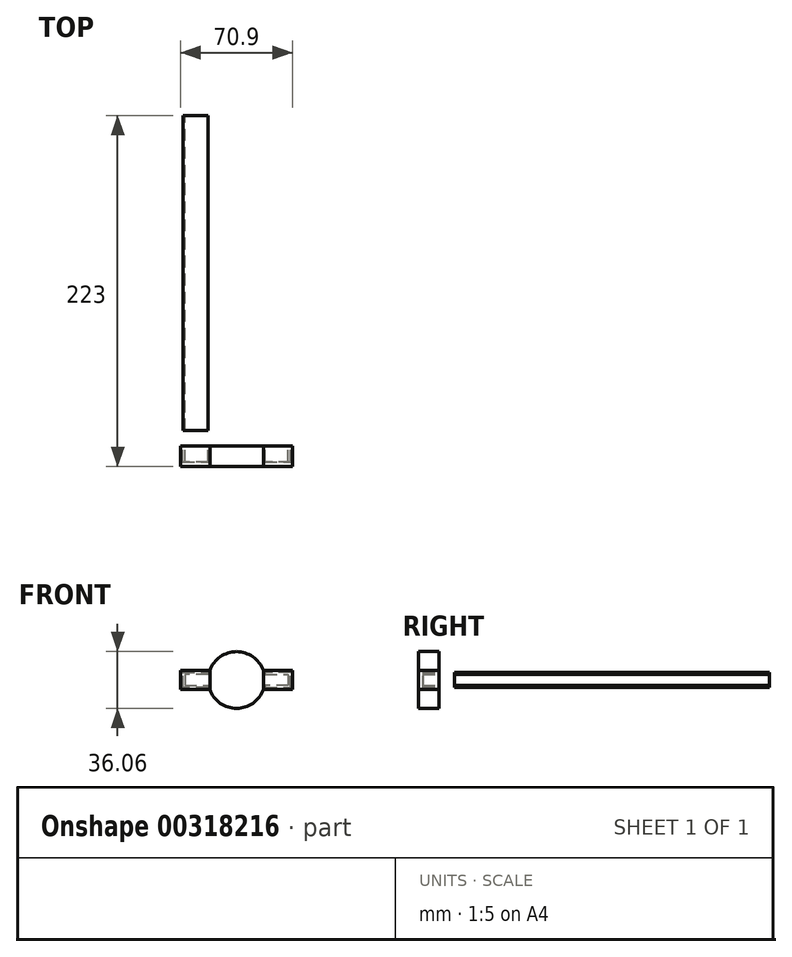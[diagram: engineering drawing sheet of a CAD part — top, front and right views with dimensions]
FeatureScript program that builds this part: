
annotation { "Feature Type Name" : "Feature", "Feature Type Description" : "" }
export const myFeature = defineFeature(function(context is Context, id is Id, definition is map)
    precondition{}
    {
        {
            var Q0;
            Q0=qCreatedBy(makeId("Front.planeOp"),FACE);
            var sketch = newSketch(context, id + "F0", { "sketchPlane" : qUnion([Q0])});
            skLineSegment(sketch, "E0", {"start": v(-34.15, 33.2) * mm, "end": v(-18.28, 33.2) * mm});
            skLineSegment(sketch, "E1", {"start": v(-18.28, 33.2) * mm, "end": v(-18.28, 31.9) * mm});
            skLineSegment(sketch, "E2", {"start": v(-18.28, 31.9) * mm, "end": v(-32.85, 31.9) * mm});
            skLineSegment(sketch, "E3", {"start": v(-32.85, 31.9) * mm, "end": v(-32.85, 24.98) * mm});
            skLineSegment(sketch, "E4", {"start": v(-32.85, 24.98) * mm, "end": v(-18.28, 24.98) * mm});
            skLineSegment(sketch, "E5", {"start": v(-18.28, 24.98) * mm, "end": v(-18.28, 23.68) * mm});
            skLineSegment(sketch, "E6", {"start": v(-18.28, 23.68) * mm, "end": v(-34.15, 23.68) * mm});
            skLineSegment(sketch, "E7", {"start": v(-34.15, 23.68) * mm, "end": v(-34.15, 33.2) * mm});
            skLineSegment(sketch, "E8", {"start": v(-34.15, 28.44) * mm, "end": v(-32.85, 28.44) * mm, "construction": true});
            skSolve(sketch);
        }
        {
            var Q0;
            Q0=qSketchRegion(id+"F0",true);
            extrude(context, id + "F1", {"entities" : qUnion([Q0]), "endBound" : BoundingType.SYMMETRIC, "depth" : 200 * mm});
        }
        {
            var Q0;
            Q0=makeQuery(id+"F1.opExtrude","CAP_FACE",FACE,{"disambiguationData":[OSD([sQuery(id+"F0.wireOp",EDGE,"E0"),sQuery(id+"F0.wireOp",EDGE,"E1"),sQuery(id+"F0.wireOp",EDGE,"E2"),sQuery(id+"F0.wireOp",EDGE,"E3"),sQuery(id+"F0.wireOp",EDGE,"E4"),sQuery(id+"F0.wireOp",EDGE,"E5"),sQuery(id+"F0.wireOp",EDGE,"E6"),sQuery(id+"F0.wireOp",EDGE,"E7")])],"isStart":false});
            cPlane(context, id + "F2", {"entities" : qUnion([Q0]), "cplaneType" : CPlaneType.OFFSET, "offset" : 10 * mm, "width" : 150 * mm, "height" : 150 * mm});
        }
        {
            var Q0;
            Q0=qCreatedBy(id+"F2.planeOp",FACE);
            var sketch = newSketch(context, id + "F3", { "sketchPlane" : qUnion([Q0])});
            skLineSegment(sketch, "E9.0", {"start": v(-34.15, 33.2) * mm, "end": v(-18.28, 33.2) * mm, "construction": true});
            skLineSegment(sketch, "E10.0", {"start": v(-18.28, 33.2) * mm, "end": v(-18.28, 31.9) * mm, "construction": true});
            skLineSegment(sketch, "E11.0", {"start": v(-18.28, 31.9) * mm, "end": v(-32.85, 31.9) * mm, "construction": true});
            skLineSegment(sketch, "E12.0", {"start": v(-32.85, 31.9) * mm, "end": v(-32.85, 24.98) * mm, "construction": true});
            skLineSegment(sketch, "E13.0", {"start": v(-34.15, 23.68) * mm, "end": v(-34.15, 33.2) * mm, "construction": true});
            skLineSegment(sketch, "E14.0", {"start": v(-32.85, 24.98) * mm, "end": v(-18.28, 24.98) * mm, "construction": true});
            skLineSegment(sketch, "E15.0", {"start": v(-18.28, 24.98) * mm, "end": v(-18.28, 23.68) * mm, "construction": true});
            skLineSegment(sketch, "E16.0", {"start": v(-18.28, 23.68) * mm, "end": v(-34.15, 23.68) * mm, "construction": true});
            skLineSegment(sketch, "E17", {"start": v(-34.2, 33.22) * mm, "end": v(-18.23, 33.22) * mm});
            skLineSegment(sketch, "E18", {"start": v(-18.23, 33.22) * mm, "end": v(-18.23, 31.82) * mm});
            skLineSegment(sketch, "E19", {"start": v(-18.23, 31.82) * mm, "end": v(-32.8, 31.82) * mm});
            skLineSegment(sketch, "E20", {"start": v(-32.8, 31.82) * mm, "end": v(-32.8, 25) * mm});
            skLineSegment(sketch, "E21", {"start": v(-32.8, 25) * mm, "end": v(-18.23, 25) * mm});
            skLineSegment(sketch, "E22", {"start": v(-18.23, 25) * mm, "end": v(-18.23, 23.6) * mm});
            skLineSegment(sketch, "E23", {"start": v(-18.23, 23.6) * mm, "end": v(-34.23, 23.6) * mm});
            skLineSegment(sketch, "E24", {"start": v(-34.23, 23.6) * mm, "end": v(-34.2, 33.22) * mm});
            skPoint(sketch, "E25", {"position": v(-18.23, 32.52) * mm});
            skLineSegment(sketch, "E26", {"start": v(-18.23, 32.52) * mm, "end": v(-34.2, 32.58) * mm, "construction": true});
            skLineSegment(sketch, "E27", {"start": v(-18.28, 32.55) * mm, "end": v(-34.15, 32.55) * mm, "construction": true});
            skPoint(sketch, "E28", {"position": v(-26.21, 32.55) * mm});
            skLineSegment(sketch, "E29", {"start": v(-32.8, 31.82) * mm, "end": v(-34.2, 31.82) * mm, "construction": true});
            skLineSegment(sketch, "E30.bottom", {"start": v(-35.45, 34.5) * mm, "end": v(-16.98, 34.5) * mm});
            skLineSegment(sketch, "E30.top", {"start": v(-35.45, 22.38) * mm, "end": v(-16.98, 22.38) * mm});
            skLineSegment(sketch, "E30.left", {"start": v(-35.45, 34.5) * mm, "end": v(-35.45, 22.38) * mm});
            skLineSegment(sketch, "E30.right", {"start": v(-16.98, 34.5) * mm, "end": v(-16.98, 22.38) * mm});
            skLineSegment(sketch, "E31", {"start": v(-35.45, 28.44) * mm, "end": v(-16.98, 28.44) * mm, "construction": true});
            skLineSegment(sketch, "E32", {"start": v(-26.21, 22.38) * mm, "end": v(-26.21, 34.5) * mm, "construction": true});
            skPoint(sketch, "E33", {"position": v(-32.85, 28.44) * mm});
            skSolve(sketch);
        }
        {
            var Q0;
            Q0=qSketchRegion(id+"F3",true);
            extrude(context, id + "F4", {"entities" : qUnion([Q0]), "depth" : 10 * mm});
        }
        {
            var Q0;
            Q0=makeQuery(id+"F4.opExtrude","CAP_FACE",FACE,{"disambiguationData":[OSD([sQuery(id+"F3.wireOp",EDGE,"E17"),sQuery(id+"F3.wireOp",EDGE,"E18"),sQuery(id+"F3.wireOp",EDGE,"E19"),sQuery(id+"F3.wireOp",EDGE,"E20"),sQuery(id+"F3.wireOp",EDGE,"E21"),sQuery(id+"F3.wireOp",EDGE,"E22"),sQuery(id+"F3.wireOp",EDGE,"E23"),sQuery(id+"F3.wireOp",EDGE,"E24"),sQuery(id+"F3.wireOp",EDGE,"E30.bottom"),sQuery(id+"F3.wireOp",EDGE,"E30.top"),sQuery(id+"F3.wireOp",EDGE,"E30.left"),sQuery(id+"F3.wireOp",EDGE,"E30.right")])],"isStart":false});
            var sketch = newSketch(context, id + "F5", { "sketchPlane" : qUnion([Q0])});
            skLineSegment(sketch, "E34.bottom", {"start": v(-35.45, 34.5) * mm, "end": v(-16.98, 34.5) * mm});
            skLineSegment(sketch, "E34.top", {"start": v(-35.45, 22.38) * mm, "end": v(-16.98, 22.38) * mm});
            skLineSegment(sketch, "E34.left", {"start": v(-35.45, 34.5) * mm, "end": v(-35.45, 22.38) * mm});
            skLineSegment(sketch, "E34.right", {"start": v(-16.98, 34.5) * mm, "end": v(-16.98, 22.38) * mm});
            skSolve(sketch);
        }
        {
            var Q0;
            Q0=qSketchRegion(id+"F5",true);
            extrude(context, id + "F6", {"entities" : qUnion([Q0]), "operationType" : NewBodyOperationType.ADD, "depth" : 3 * mm});
        }
        {
            var Q0;
            Q0=makeQuery(id+"F4.opExtrude","SWEPT_BODY",BODY,{"disambiguationData":[OSD([sQuery(id+"F3.wireOp",EDGE,"E17"),sQuery(id+"F3.wireOp",EDGE,"E18"),sQuery(id+"F3.wireOp",EDGE,"E19"),sQuery(id+"F3.wireOp",EDGE,"E20"),sQuery(id+"F3.wireOp",EDGE,"E21"),sQuery(id+"F3.wireOp",EDGE,"E22"),sQuery(id+"F3.wireOp",EDGE,"E23"),sQuery(id+"F3.wireOp",EDGE,"E24"),sQuery(id+"F3.wireOp",EDGE,"E30.bottom"),sQuery(id+"F3.wireOp",EDGE,"E30.top"),sQuery(id+"F3.wireOp",EDGE,"E30.left"),sQuery(id+"F3.wireOp",EDGE,"E30.right")])]});
            var Q1;
            Q1=qCreatedBy(makeId("Right.planeOp"),FACE);
            mirror(context, id + "F7", {"entities" : qUnion([Q0]), "mirrorPlane" : qUnion([Q1])});
        }
        {
            var Q0;
            Q0=makeQuery(id+"F7.opPattern","COPY",FACE,{"derivedFrom":makeQuery(id+"F6.opExtrude","CAP_FACE",FACE,{"disambiguationData":[OSD([sQuery(id+"F5.wireOp",EDGE,"E34.bottom"),sQuery(id+"F5.wireOp",EDGE,"E34.top"),sQuery(id+"F5.wireOp",EDGE,"E34.left"),sQuery(id+"F5.wireOp",EDGE,"E34.right")])],"isStart":false}),"instanceName":"1"});
            var sketch = newSketch(context, id + "F8", { "sketchPlane" : qUnion([Q0])});
            skLineSegment(sketch, "E35.0", {"start": v(-16.98, 34.5) * mm, "end": v(-16.98, 22.38) * mm});
            skLineSegment(sketch, "E36.bottom", {"start": v(16.98, 22.38) * mm, "end": v(-16.98, 22.38) * mm});
            skLineSegment(sketch, "E36.top", {"start": v(16.98, 34.5) * mm, "end": v(-16.98, 34.5) * mm});
            skLineSegment(sketch, "E36.left", {"start": v(16.98, 22.38) * mm, "end": v(16.98, 34.5) * mm});
            skLineSegment(sketch, "E36.right", {"start": v(-16.98, 22.38) * mm, "end": v(-16.98, 34.5) * mm});
            skArc(sketch, "E37", {"start": v(-16.98, 22.38) * mm, "mid": v(0, 10.41) * mm, "end": v(16.98, 22.38) * mm});
            skArc(sketch, "E38", {"start": v(16.98, 34.5) * mm, "mid": v(0, 46.47) * mm, "end": v(-16.98, 34.5) * mm});
            skLineSegment(sketch, "E39", {"start": v(16.98, 28.44) * mm, "end": v(-16.98, 28.44) * mm, "construction": true});
            skSolve(sketch);
        }
        {
            var Q0;
            Q0=qSketchRegion(id+"F8",true);
            var Q1;
            Q1=makeQuery(id+"F7.opPattern","COPY",FACE,{"derivedFrom":makeQuery(id+"F4.opExtrude","CAP_FACE",FACE,{"disambiguationData":[OSD([sQuery(id+"F3.wireOp",EDGE,"E17"),sQuery(id+"F3.wireOp",EDGE,"E18"),sQuery(id+"F3.wireOp",EDGE,"E19"),sQuery(id+"F3.wireOp",EDGE,"E20"),sQuery(id+"F3.wireOp",EDGE,"E21"),sQuery(id+"F3.wireOp",EDGE,"E22"),sQuery(id+"F3.wireOp",EDGE,"E23"),sQuery(id+"F3.wireOp",EDGE,"E24"),sQuery(id+"F3.wireOp",EDGE,"E30.bottom"),sQuery(id+"F3.wireOp",EDGE,"E30.top"),sQuery(id+"F3.wireOp",EDGE,"E30.left"),sQuery(id+"F3.wireOp",EDGE,"E30.right")])],"isStart":true}),"instanceName":"1"});
            extrude(context, id + "F9", {"entities" : qUnion([Q0]), "endBound" : BoundingType.UP_TO_SURFACE, "oppositeDirection" : true, "endBoundEntityFace" : qUnion([Q1]), "depth" : 25 * mm});
        }
    });
